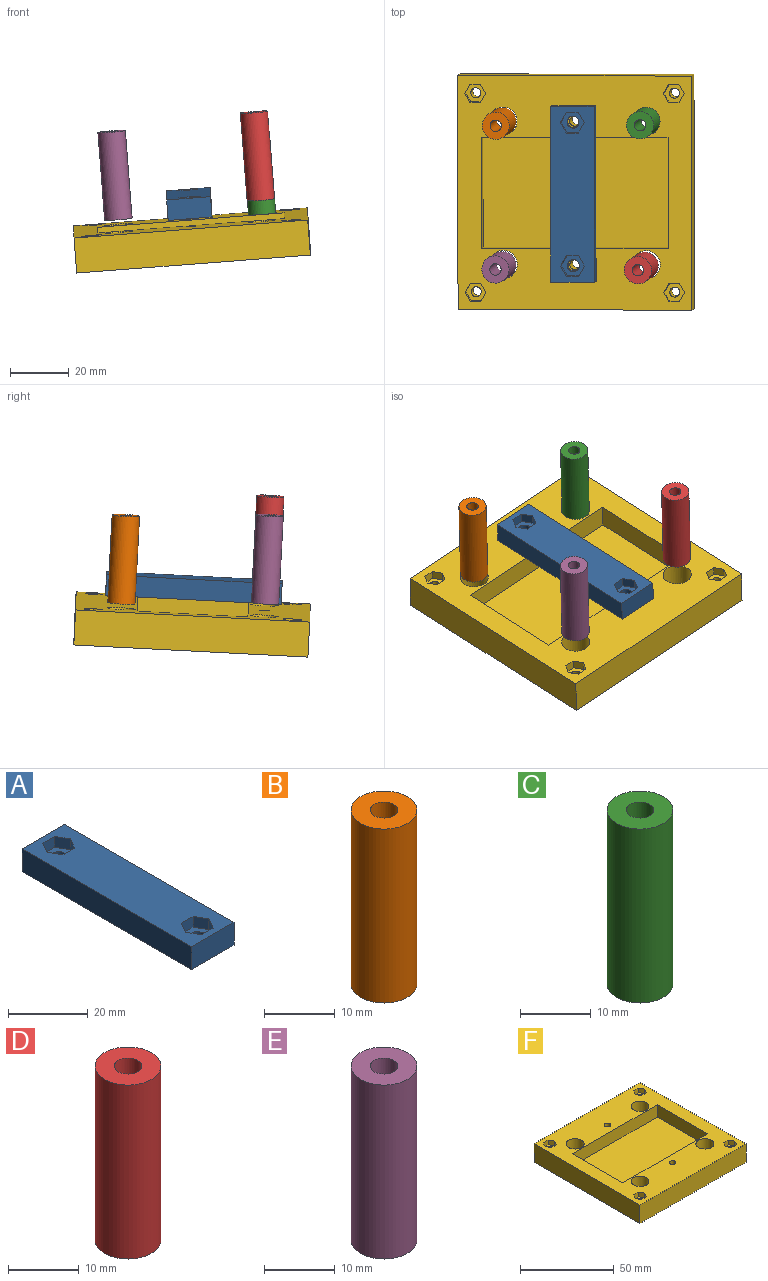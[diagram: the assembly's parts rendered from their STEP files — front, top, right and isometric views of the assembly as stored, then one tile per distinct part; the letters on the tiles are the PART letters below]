
ASSEMBLY  parts=6 mates=5
PART A: 22 faces, bbox 15x60x7 mm
  f0: plane 3.55x3.3mm, normal (-0.87,-0.5,0), area 13.5mm2, adj f1,f15,f16,f19
  f1: plane 3.55x3.3mm, normal (-0.87,0.5,0), area 13.5mm2, adj f0,f2,f16,f19
  f2: plane 4.1x3.3mm, normal (0,1,0), area 13.5mm2, adj f1,f3,f16,f19
  f3: plane 3.55x3.3mm, normal (0.87,0.5,0), area 13.5mm2, adj f2,f4,f16,f19
  f4: plane 3.55x3.3mm, normal (0.87,-0.5,0), area 13.5mm2, adj f3,f15,f16,f19
  f5: plane 15x7mm, normal (0,-1,0), area 105mm2, adj f6,f13,f16,f17
  f6: plane 60x7mm, normal (1,0,0), area 420mm2, adj f5,f7,f16,f17
  f7: plane 15x7mm, normal (0,1,0), area 105mm2, adj f6,f13,f16,f17
  f8: plane 3.55x3.3mm, normal (-0.87,0.5,0), area 13.5mm2, adj f9,f14,f16,f21
  f9: plane 4.1x3.3mm, normal (0,1,0), area 13.5mm2, adj f8,f10,f16,f21
  f10: plane 3.55x3.3mm, normal (0.87,0.5,0), area 13.5mm2, adj f9,f11,f16,f21
  f11: plane 3.55x3.3mm, normal (0.87,-0.5,0), area 13.5mm2, adj f10,f12,f16,f21
  f12: plane 4.1x3.3mm, normal (0,-1,0), area 13.5mm2, adj f11,f14,f16,f21
  f13: plane 60x7mm, normal (-1,0,0), area 420mm2, adj f5,f7,f16,f17
  f14: plane 3.55x3.3mm, normal (-0.87,-0.5,0), area 13.5mm2, adj f8,f12,f16,f21
  f15: plane 4.1x3.3mm, normal (0,-1,0), area 13.5mm2, adj f0,f4,f16,f19
  f16: plane 60x15mm, normal (0,0,1), area 812.7mm2, adj f0,f1,f2,f3,f4,f5,f6,f7
  f17: plane 60x15mm, normal (0,0,-1), area 873.6mm2, adj f5,f6,f7,f13,f18,f20
  f18: cylinder r=2.05mm len=4.1mm, axis (0,0,-1), area 47.7mm2, adj f17,f19
  f19: plane 8.2x7.1mm, normal (0,0,1), area 30.5mm2, adj f0,f1,f2,f3,f4,f15,f18
  f20: cylinder r=2.05mm len=4.1mm, axis (0,0,-1), area 47.7mm2, adj f17,f21
  f21: plane 8.2x7.1mm, normal (0,0,1), area 30.5mm2, adj f8,f9,f10,f11,f12,f14,f20
PART B: 4 faces, bbox 9.3x9.3x30 mm
  f0: cylinder r=4.65mm len=30mm, axis (0,0,-1), area 876.5mm2, adj f1,f2
  f1: plane 9.3x9.3mm, normal (0,0,1), area 56mm2, adj f0,f3
  f2: plane 9.3x9.3mm, normal (0,0,-1), area 56mm2, adj f0,f3
  f3: cylinder r=1.95mm len=30mm, axis (0,0,-1), area 367.6mm2, adj f1,f2
PART C: 4 faces, bbox 9.3x9.3x30 mm
  f0: cylinder r=1.95mm len=30mm, axis (0,0,-1), area 367.6mm2, adj f1,f2
  f1: plane 9.3x9.3mm, normal (0,0,1), area 56mm2, adj f0,f3
  f2: plane 9.3x9.3mm, normal (0,0,-1), area 56mm2, adj f0,f3
  f3: cylinder r=4.65mm len=30mm, axis (0,0,-1), area 876.5mm2, adj f1,f2
PART D: 4 faces, bbox 9.3x9.3x30 mm
  f0: cylinder r=4.65mm len=30mm, axis (0,0,-1), area 876.5mm2, adj f1,f2
  f1: plane 9.3x9.3mm, normal (0,0,1), area 56mm2, adj f0,f3
  f2: plane 9.3x9.3mm, normal (0,0,-1), area 56mm2, adj f0,f3
  f3: cylinder r=1.95mm len=30mm, axis (0,0,-1), area 367.6mm2, adj f1,f2
PART E: 4 faces, bbox 9.3x9.3x30 mm
  f0: cylinder r=4.65mm len=30mm, axis (0,0,-1), area 876.5mm2, adj f1,f2
  f1: plane 9.3x9.3mm, normal (0,0,1), area 56mm2, adj f0,f3
  f2: plane 9.3x9.3mm, normal (0,0,-1), area 56mm2, adj f0,f3
  f3: cylinder r=1.95mm len=30mm, axis (0,0,-1), area 367.6mm2, adj f1,f2
PART F: 49 faces, bbox 80x80x12 mm
  f0: plane 80x12mm, normal (0,-1,0), area 960mm2, adj f1,f37,f38,f39
  f1: plane 80x12mm, normal (1,0,0), area 960mm2, adj f0,f2,f38,f39
  f2: plane 80x12mm, normal (0,1,0), area 960mm2, adj f1,f37,f38,f39
  f3: plane 3.1x3mm, normal (-0.87,-0.5,0), area 10.7mm2, adj f4,f26,f38,f46
  f4: plane 3.1x3mm, normal (-0.87,0.5,0), area 10.7mm2, adj f3,f5,f38,f46
  f5: plane 3.58x3mm, normal (0,1,0), area 10.7mm2, adj f4,f6,f38,f46
  f6: plane 3.1x3mm, normal (0.87,0.5,0), area 10.7mm2, adj f5,f7,f38,f46
  f7: plane 3.1x3mm, normal (0.87,-0.5,0), area 10.7mm2, adj f6,f26,f38,f46
  f8: plane 3.1x3mm, normal (0.87,-0.5,0), area 10.7mm2, adj f9,f33,f38,f48
  f9: plane 3.58x3mm, normal (0,-1,0), area 10.7mm2, adj f8,f10,f38,f48
  f10: plane 3.1x3mm, normal (-0.87,-0.5,0), area 10.7mm2, adj f9,f11,f38,f48
  f11: plane 3.1x3mm, normal (-0.87,0.5,0), area 10.7mm2, adj f10,f12,f38,f48
  f12: plane 3.58x3mm, normal (0,1,0), area 10.7mm2, adj f11,f33,f38,f48
  f13: plane 3.1x3mm, normal (-0.87,0.5,0), area 10.7mm2, adj f14,f34,f38,f44
  f14: plane 3.58x3mm, normal (0,1,0), area 10.7mm2, adj f13,f15,f38,f44
  f15: plane 3.1x3mm, normal (0.87,0.5,0), area 10.7mm2, adj f14,f16,f38,f44
  f16: plane 3.1x3mm, normal (0.87,-0.5,0), area 10.7mm2, adj f15,f17,f38,f44
  f17: plane 3.58x3mm, normal (0,-1,0), area 10.7mm2, adj f16,f34,f38,f44
  f18: plane 3.1x3mm, normal (-0.87,0.5,0), area 10.7mm2, adj f19,f35,f38,f42
  f19: plane 3.58x3mm, normal (0,1,0), area 10.7mm2, adj f18,f20,f38,f42
  f20: plane 3.1x3mm, normal (0.87,0.5,0), area 10.7mm2, adj f19,f21,f38,f42
  f21: plane 3.1x3mm, normal (0.87,-0.5,0), area 10.7mm2, adj f20,f22,f38,f42
  f22: plane 3.58x3mm, normal (0,-1,0), area 10.7mm2, adj f21,f35,f38,f42
  f23: plane 38x8mm, normal (-1,0,0), area 304mm2, adj f24,f36,f38,f40
  f24: plane 64x8mm, normal (0,1,0), area 512mm2, adj f23,f25,f38,f40
  f25: plane 38x8mm, normal (1,0,0), area 304mm2, adj f24,f36,f38,f40
  f26: plane 3.58x3mm, normal (0,-1,0), area 10.7mm2, adj f3,f7,f38,f46
  f27: cylinder r=1.7mm len=12mm, axis (0,0,-1), area 128.2mm2, adj f38,f39
  f28: cylinder r=1.7mm len=12mm, axis (0,0,-1), area 128.2mm2, adj f38,f39
  f29: cylinder r=4.8mm len=12mm, axis (0,0,-1), area 361.9mm2, adj f38,f39
  f30: cylinder r=4.8mm len=12mm, axis (0,0,-1), area 361.9mm2, adj f38,f39
  f31: cylinder r=4.8mm len=12mm, axis (0,0,-1), area 361.9mm2, adj f38,f39
  f32: cylinder r=4.8mm len=12mm, axis (0,0,-1), area 361.9mm2, adj f38,f39
  f33: plane 3.1x3mm, normal (0.87,0.5,0), area 10.7mm2, adj f8,f12,f38,f48
  f34: plane 3.1x3mm, normal (-0.87,-0.5,0), area 10.7mm2, adj f13,f17,f38,f44
  f35: plane 3.1x3mm, normal (-0.87,-0.5,0), area 10.7mm2, adj f18,f22,f38,f42
  f36: plane 64x8mm, normal (0,-1,0), area 512mm2, adj f23,f25,f38,f40
  f37: plane 80x12mm, normal (-1,0,0), area 960mm2, adj f0,f2,f38,f39
  f38: plane 80x80mm, normal (0,0,1), area 3527.2mm2, adj f0,f1,f2,f3,f4,f5,f6,f7
  f39: plane 80x80mm, normal (0,0,-1), area 6056mm2, adj f0,f1,f2,f27,f28,f29,f30,f31
  f40: plane 64x38mm, normal (0,0,1), area 2432mm2, adj f23,f24,f25,f36
  f41: cylinder r=1.7mm len=9mm, axis (0,0,-1), area 96.1mm2, adj f39,f42
  f42: plane 7.16x6.2mm, normal (0,0,1), area 24.2mm2, adj f18,f19,f20,f21,f22,f35,f41
  f43: cylinder r=1.7mm len=9mm, axis (0,0,-1), area 96.1mm2, adj f39,f44
  f44: plane 7.16x6.2mm, normal (0,0,1), area 24.2mm2, adj f13,f14,f15,f16,f17,f34,f43
  f45: cylinder r=1.7mm len=9mm, axis (0,0,-1), area 96.1mm2, adj f39,f46
  f46: plane 7.16x6.2mm, normal (0,0,1), area 24.2mm2, adj f3,f4,f5,f6,f7,f26,f45
  f47: cylinder r=1.7mm len=9mm, axis (0,0,-1), area 96.1mm2, adj f39,f48
  f48: plane 7.16x6.2mm, normal (0,0,1), area 24.2mm2, adj f8,f9,f10,f11,f12,f33,f47
PLACE A rot(axis=(0.56,-0.83,0),5.3deg) t=(164.96,-7.04,34.45)mm
PLACE B rot(axis=(0.56,-0.83,0),5.3deg) t=(164.94,41.95,35.94)mm
PLACE C rot(axis=(0.56,-0.83,0),5.3deg) t=(165.43,-6.72,28.34)mm
PLACE D rot(axis=(0.56,-0.83,0),5.3deg) t=(213.57,-56.3,40)mm
PLACE E rot(axis=(0.56,-0.83,0),5.3deg) t=(115.99,-7.02,32.16)mm
PLACE F rot(axis=(0.56,-0.83,0),5.3deg) t=(166.11,-6.26,19.49)mm
MATE slider A.f20 <-> F.f28  axis (0.08,0.05,-1) through (165,-31.51,33.18)mm
MATE slider E.f0 <-> F.f29  axis (0.08,0.05,-1) through (140.46,-31.54,32.77)mm
MATE slider C.f0 <-> F.f30  axis (0.08,0.05,-1) through (189.81,17.69,31.49)mm
MATE slider B.f0 <-> F.f31  axis (0.08,0.05,-1) through (140.56,17.53,32.78)mm
MATE slider D.f0 <-> F.f32  axis (0.08,0.05,-1) through (189.1,-31.78,39.39)mm
